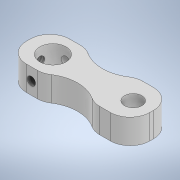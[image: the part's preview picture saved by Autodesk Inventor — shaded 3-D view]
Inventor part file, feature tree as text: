
AUTODESK INVENTOR PART (.ipt)
format: ipt  version: 2021.2 (Build 252289000, 289)  size: 180,736 bytes
history: native  units: in
note: dims shown in document units (in); Inventor stores cm internally (conversion verified against a paired STEP export)
features: sketch x6, hole x4, extrude x2, fillet x2
ambient origin geometry x8: Origin, YZ Plane, XZ Plane, XY Plane, X Axis, Y Axis, Z Axis, Center Point
bodies: Solid1 (feature_tree)
feature tree (14):
  extrude  "Extrusion1"  Depth=0.4375in
  hole  "Hole1"  [1 undecoded]
  hole  "Hole2"  [1 undecoded]
  fillet  "Fillet1"  Radius=0.2188in
  extrude  "Extrusion2"  Depth=0.2in
  fillet  "Fillet2"  Radius=0.5in
  hole  "Hole3"  [1 undecoded]
  hole  "Hole4"  [1 undecoded]
  sketch  "Sketch1"  dims[d0=1.25in d1=0.4375in]
  sketch  "Sketch2"  dims[d2=0.25in d3=0.0in d4=0.1875in]
  sketch  "Sketch3"  dims[d5=0.2188in]
  sketch  "Sketch4"  dims[d6=0.177in d7=0.328in d8=0.332in d9=0.25in d10=0.5635in d11=0.484in d12=0.0in d13=0.25in d14=0.2188in]
  sketch  "Sketch5"  dims[d15=0.266in d16=0.328in d17=0.507in d18=0.25in d19=0.5635in d20=0.484in d21=0.0in d22=0.2in d23=0.5in]
  sketch  "Sketch6"  dims[d24=0.5in d25=0.25in d26=0.0in d27=0.2in d28=0.125in d29=0.25in d30=0.0849in d31=0.224in d32=0.507in d33=0.25in d34=0.5635in d35=0.349in d36=0.0in d37=0.125in d38=0.2176in d39=0.0849in d40=0.2in d41=0.507in d42=0.25in d43=0.5635in d44=0.2in d45=0.0in]
note: 4 required parameter values undecoded (feature->parameter linkage not recoverable at this tier; creation-order binding heuristic only, values carry confidence <= 0.55)
